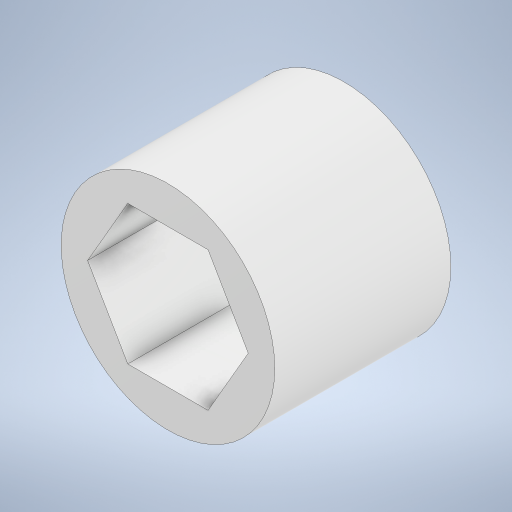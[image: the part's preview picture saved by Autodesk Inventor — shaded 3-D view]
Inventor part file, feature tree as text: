
AUTODESK INVENTOR PART (.ipt)
format: ipt  version: 2024 (Build 280153000, 153)  size: 224,768 bytes
history: native  units: in
note: dims shown in document units (in); Inventor stores cm internally (conversion verified against a paired STEP export)
features: extrude x1, sketch x1
ambient origin geometry x8: Origin, YZ Plane, XZ Plane, XY Plane, X Axis, Y Axis, Z Axis, Center Point
bodies: Solid1 (feature_tree)
feature tree (2):
  extrude  "Extrusion1"  Depth=0.5in
  sketch  "Sketch1"  dims[d0=0.7677in d1=0.5in d2=0.633in d3=0.0in]
